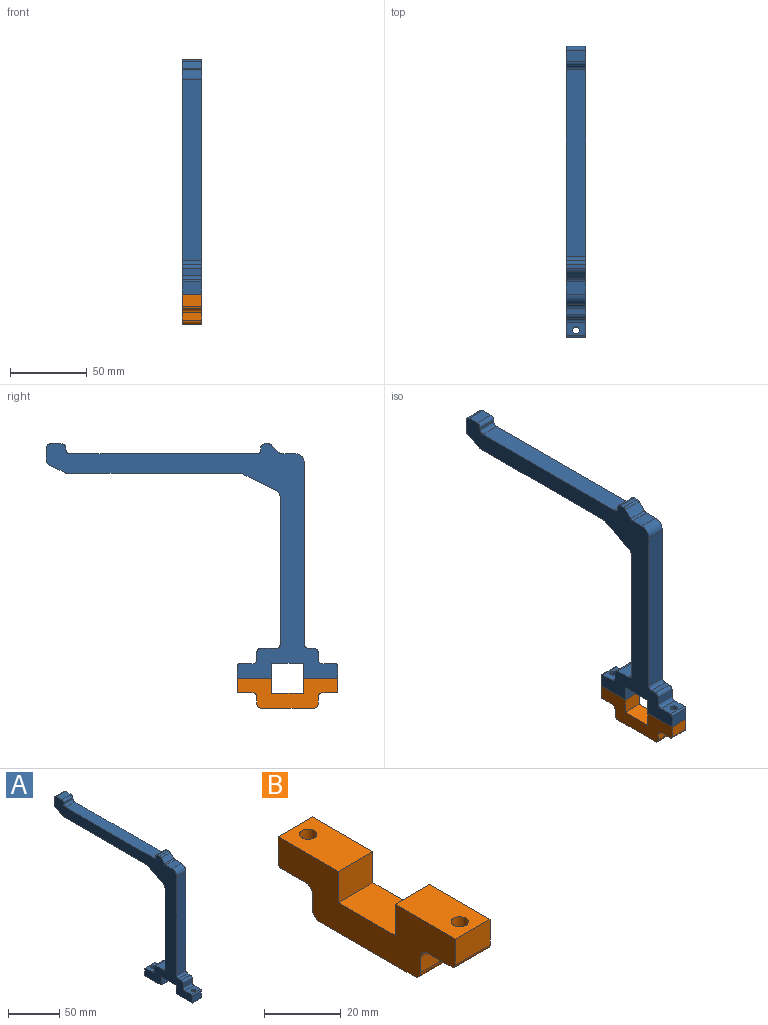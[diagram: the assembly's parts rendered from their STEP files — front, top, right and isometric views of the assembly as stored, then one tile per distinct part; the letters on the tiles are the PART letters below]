
ASSEMBLY  parts=2 mates=1
PART A: 50 faces, bbox 12.7x189.8x152.8 mm
  f0: plane 12.7x8.47mm, normal (0,0,1), area 107.6mm2, adj f18,f19,f35,f49
  f1: plane 95.92x12.7mm, normal (0,1,0), area 1218.2mm2, adj f18,f19,f24,f37
  f2: plane 112.5x12.7mm, normal (0,0,-1), area 1428.8mm2, adj f18,f19,f36,f41
  f3: plane 12.7x8.26mm, normal (0,-1,0), area 104.8mm2, adj f4,f18,f19,f29
  f4: plane 22.23x12.7mm, normal (0,0,-1), area 266.4mm2, adj f3,f5,f18,f19,f20
  f5: plane 12.7x9.91mm, normal (0,1,0), area 125.8mm2, adj f4,f6,f18,f19
  f6: plane 20.83x12.7mm, normal (0,0,-1), area 264.5mm2, adj f5,f7,f18,f19
  f7: plane 12.7x9.91mm, normal (0,-1,0), area 125.8mm2, adj f6,f8,f18,f19
  f8: plane 22.23x12.7mm, normal (0,0,-1), area 266.4mm2, adj f7,f9,f18,f19,f21
  f9: plane 12.7x8.26mm, normal (0,1,0), area 104.8mm2, adj f8,f18,f19,f28
  f10: plane 12.7x8.89mm, normal (0,0,1), area 97mm2, adj f18,f19,f21,f22,f28
  f11: plane 12.7x4.83mm, normal (0,1,0), area 61.3mm2, adj f18,f19,f22,f23
  f12: plane 12.7x10.1mm, normal (0,0,1), area 128.2mm2, adj f18,f19,f23,f24
  f13: plane 121.92x12.7mm, normal (0,0,1), area 1548.4mm2, adj f18,f19,f42,f48
  f14: plane 118.11x12.7mm, normal (0,-1,0), area 1500mm2, adj f18,f19,f25,f35
  f15: plane 12.7x3.75mm, normal (0,0,1), area 47.6mm2, adj f18,f19,f25,f26
  f16: plane 12.7x4.83mm, normal (0,-1,0), area 61.3mm2, adj f18,f19,f26,f27
  f17: plane 12.7x8.89mm, normal (0,0,1), area 97mm2, adj f18,f19,f20,f27,f29
  f18: plane 189.8x152.78mm, normal (1,0,0), area 5017.6mm2, adj f0,f1,f2,f3,f4,f5,f6,f7
  f19: plane 189.8x152.78mm, normal (-1,0,0), area 5017.6mm2, adj f0,f1,f2,f3,f4,f5,f6,f7
  f20: cylinder r=2.25mm len=9.53mm, axis (0,0,1), area 134.7mm2, adj f4,f17
  f21: cylinder r=2.25mm len=9.53mm, axis (0,0,1), area 134.7mm2, adj f8,f10
  f22: cylinder r=2.54mm len=12.7mm, axis (1,0,0), area 50.7mm2, adj f10,f11,f18,f19
  f23: cylinder r=2.54mm len=12.7mm, axis (1,0,0), area 50.7mm2, adj f11,f12,f18,f19
  f24: cylinder r=2.54mm len=12.7mm, axis (1,0,0), area 50.7mm2, adj f1,f12,f18,f19
  f25: cylinder r=2.54mm len=12.7mm, axis (-1,0,0), area 50.7mm2, adj f14,f15,f18,f19
  f26: cylinder r=2.54mm len=12.7mm, axis (-1,0,0), area 50.7mm2, adj f15,f16,f18,f19
  f27: cylinder r=2.54mm len=12.7mm, axis (1,0,0), area 50.7mm2, adj f16,f17,f18,f19
  f28: cylinder r=1.27mm len=12.7mm, axis (-1,0,0), area 25.3mm2, adj f9,f10,f18,f19
  f29: cylinder r=1.27mm len=12.7mm, axis (-1,0,0), area 25.3mm2, adj f3,f17,f18,f19
  f30: plane 21.52x12.7mm, normal (0,0.45,-0.89), area 305.6mm2, adj f18,f19,f36,f37
  f31: plane 12.7x1.27mm, normal (0,-1,0), area 16.1mm2, adj f18,f19,f40,f42
  f32: plane 12.7x10.76mm, normal (0,0.45,-0.89), area 152.8mm2, adj f18,f19,f38,f41
  f33: plane 12.7x8.59mm, normal (0,1,0), area 109.1mm2, adj f18,f19,f38,f39
  f34: plane 12.7x7.62mm, normal (0,0,1), area 96.8mm2, adj f18,f19,f39,f40
  f35: cylinder r=6.35mm len=12.7mm, axis (-1,0,0), area 126.7mm2, adj f0,f14,f18,f19
  f36: cylinder r=5.08mm len=12.7mm, axis (-1,0,0), area 29.9mm2, adj f2,f18,f19,f30
  f37: cylinder r=5.08mm len=12.7mm, axis (1,0,0), area 71.4mm2, adj f1,f18,f19,f30
  f38: cylinder r=2.54mm len=12.7mm, axis (1,0,0), area 35.7mm2, adj f18,f19,f32,f33
  f39: cylinder r=2.54mm len=12.7mm, axis (1,0,0), area 50.7mm2, adj f18,f19,f33,f34
  f40: cylinder r=2.54mm len=12.7mm, axis (1,0,0), area 50.7mm2, adj f18,f19,f31,f34
  f41: cylinder r=2.54mm len=12.7mm, axis (-1,0,0), area 15mm2, adj f2,f18,f19,f32
  f42: cylinder r=2.54mm len=12.7mm, axis (1,0,0), area 50.7mm2, adj f13,f18,f19,f31
  f43: plane 12.7x1.27mm, normal (0,1,0), area 16.1mm2, adj f18,f19,f46,f48
  f44: plane 12.7x2.76mm, normal (0,0,1), area 35mm2, adj f18,f19,f46,f47
  f45: plane 12.7x4.86mm, normal (0,-0.71,0.71), area 87.3mm2, adj f18,f19,f47,f49
  f46: cylinder r=2.54mm len=12.7mm, axis (-1,0,0), area 50.7mm2, adj f18,f19,f43,f44
  f47: cylinder r=2.54mm len=12.7mm, axis (1,0,0), area 25.3mm2, adj f18,f19,f44,f45
  f48: cylinder r=2.54mm len=12.7mm, axis (-1,0,0), area 50.7mm2, adj f13,f18,f19,f43
  f49: cylinder r=2.54mm len=12.7mm, axis (1,0,0), area 25.3mm2, adj f0,f18,f19,f45
PART B: 22 faces, bbox 12.7x65.3x19.4 mm
  f0: plane 20.83x12.7mm, normal (0,0,1), area 264.5mm2, adj f1,f11,f12,f13
  f1: plane 12.7x9.91mm, normal (0,1,0), area 125.8mm2, adj f0,f2,f12,f13
  f2: plane 22.23x12.7mm, normal (0,0,1), area 266.4mm2, adj f1,f3,f12,f13,f15
  f3: plane 12.7x8.26mm, normal (0,-1,0), area 104.8mm2, adj f2,f12,f13,f20
  f4: plane 12.7x8.89mm, normal (0,0,-1), area 97mm2, adj f12,f13,f15,f16,f20
  f5: plane 12.7x4.83mm, normal (0,-1,0), area 61.3mm2, adj f12,f13,f16,f17
  f6: plane 34.8x12.7mm, normal (0,0,-1), area 441.9mm2, adj f12,f13,f17,f18
  f7: plane 12.7x4.83mm, normal (0,1,0), area 61.3mm2, adj f12,f13,f18,f19
  f8: plane 12.7x8.89mm, normal (0,0,-1), area 97mm2, adj f12,f13,f14,f19,f21
  f9: plane 12.7x8.26mm, normal (0,1,0), area 104.8mm2, adj f10,f12,f13,f21
  f10: plane 22.23x12.7mm, normal (0,0,1), area 266.4mm2, adj f9,f11,f12,f13,f14
  f11: plane 12.7x9.91mm, normal (0,-1,0), area 125.8mm2, adj f0,f10,f12,f13
  f12: plane 65.28x19.43mm, normal (1,0,0), area 809.8mm2, adj f0,f1,f2,f3,f4,f5,f6,f7
  f13: plane 65.28x19.43mm, normal (-1,0,0), area 809.8mm2, adj f0,f1,f2,f3,f4,f5,f6,f7
  f14: cylinder r=2.25mm len=9.53mm, axis (0,0,-1), area 134.7mm2, adj f8,f10
  f15: cylinder r=2.25mm len=9.53mm, axis (0,0,-1), area 134.7mm2, adj f2,f4
  f16: cylinder r=2.54mm len=12.7mm, axis (1,0,0), area 50.7mm2, adj f4,f5,f12,f13
  f17: cylinder r=2.54mm len=12.7mm, axis (-1,0,0), area 50.7mm2, adj f5,f6,f12,f13
  f18: cylinder r=2.54mm len=12.7mm, axis (1,0,0), area 50.7mm2, adj f6,f7,f12,f13
  f19: cylinder r=2.54mm len=12.7mm, axis (1,0,0), area 50.7mm2, adj f7,f8,f12,f13
  f20: cylinder r=1.27mm len=12.7mm, axis (-1,0,0), area 25.3mm2, adj f3,f4,f12,f13
  f21: cylinder r=1.27mm len=12.7mm, axis (-1,0,0), area 25.3mm2, adj f8,f9,f12,f13
PLACE A t=(-63.75,8.75,20.24)mm
PLACE B t=(-63.75,-39.66,-2.55)mm
MATE fastened B.f15 <-> A.f20  axis (0,0,1) through (-57.4,-67.53,7.36)mm
